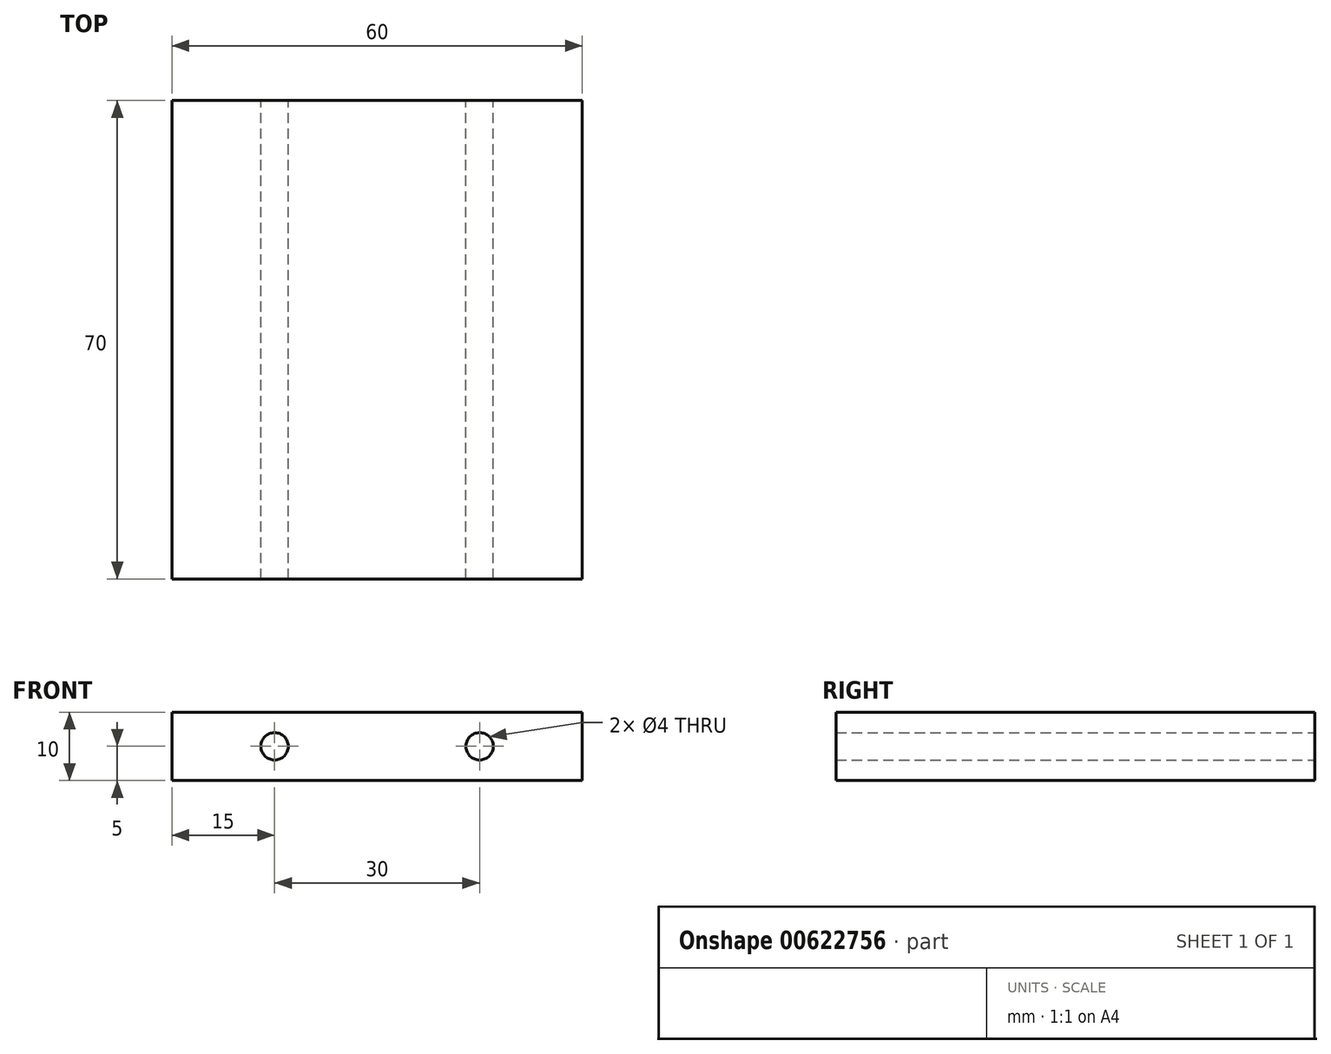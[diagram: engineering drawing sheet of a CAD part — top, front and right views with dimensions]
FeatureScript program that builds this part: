
annotation { "Feature Type Name" : "Feature", "Feature Type Description" : "" }
export const myFeature = defineFeature(function(context is Context, id is Id, definition is map)
    precondition{}
    {
        {
            var Q0;
            Q0=qCreatedBy(makeId("Front.planeOp"),FACE);
            var sketch = newSketch(context, id + "F0", { "sketchPlane" : qUnion([Q0])});
            skLineSegment(sketch, "E0.bottom", {"start": v(0, 0) * mm, "end": v(60, 0) * mm});
            skLineSegment(sketch, "E0.top", {"start": v(0, 10) * mm, "end": v(60, 10) * mm});
            skLineSegment(sketch, "E0.left", {"start": v(0, 0) * mm, "end": v(0, 10) * mm});
            skLineSegment(sketch, "E0.right", {"start": v(60, 0) * mm, "end": v(60, 10) * mm});
            skCircle(sketch, "E1", {"center": v(15, 5) * mm, "radius": 2 * mm});
            skCircle(sketch, "E2", {"center": v(45, 5) * mm, "radius": 2 * mm});
            skSolve(sketch);
        }
        {
            var Q0;
            Q0=makeQuery(id+"F0.imprint","IMPRINT",FACE,{"disambiguationData":[TD([[makeQuery(id+"F0.imprint","IMPRINT",EDGE,{"derivedFrom":sQuery(id+"F0.wireOp",EDGE,"E0.bottom")}),1.0]])]});
            extrude(context, id + "F1", {"entities" : qUnion([Q0]), "depth" : 70 * mm, "offsetDistance" : 25.4 * mm});
        }
    });
